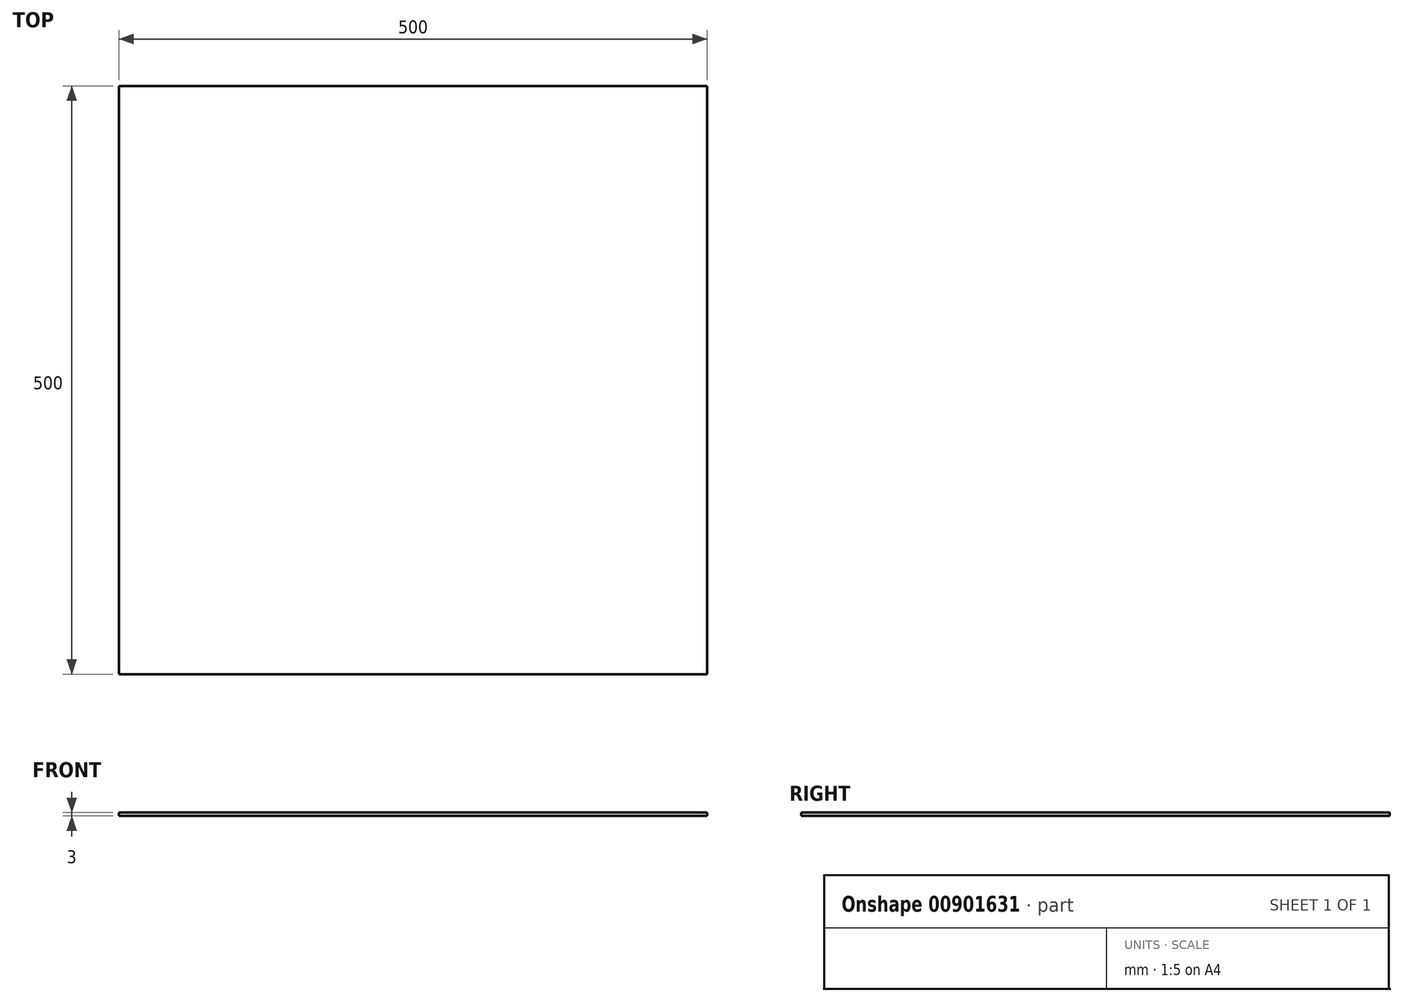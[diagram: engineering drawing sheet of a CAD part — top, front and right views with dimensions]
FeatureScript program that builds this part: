
annotation { "Feature Type Name" : "Feature", "Feature Type Description" : "" }
export const myFeature = defineFeature(function(context is Context, id is Id, definition is map)
    precondition{}
    {
        {
            assignVariable(context, id + "F0", {"name" : "glass_W", "anyValue" : 3});
        }
        {
            var Q0;
            Q0=qCreatedBy(makeId("Top.planeOp"),FACE);
            var sketch = newSketch(context, id + "F1", { "sketchPlane" : qUnion([Q0])});
            skLineSegment(sketch, "E0.bottom", {"start": v(-250, 250) * mm, "end": v(250, 250) * mm});
            skLineSegment(sketch, "E0.top", {"start": v(-250, -250) * mm, "end": v(250, -250) * mm});
            skLineSegment(sketch, "E0.left", {"start": v(-250, 250) * mm, "end": v(-250, -250) * mm});
            skLineSegment(sketch, "E0.right", {"start": v(250, 250) * mm, "end": v(250, -250) * mm});
            skPoint(sketch, "E0.middle", {"position": v(0, 0) * mm});
            skSolve(sketch);
        }
        {
            var Q0;
            Q0=makeQuery(id+"F1.imprint","IMPRINT",FACE,{"disambiguationData":[TD([[makeQuery(id+"F1.imprint","IMPRINT",EDGE,{"derivedFrom":sQuery(id+"F1.wireOp",EDGE,"E0.bottom")}),-1.0]])]});
            extrude(context, id + "F2", {"entities" : qUnion([Q0]), "depth" : (getVariable(context, 'glass_W')) * mm, "offsetDistance" : 25 * mm});
        }
    });
